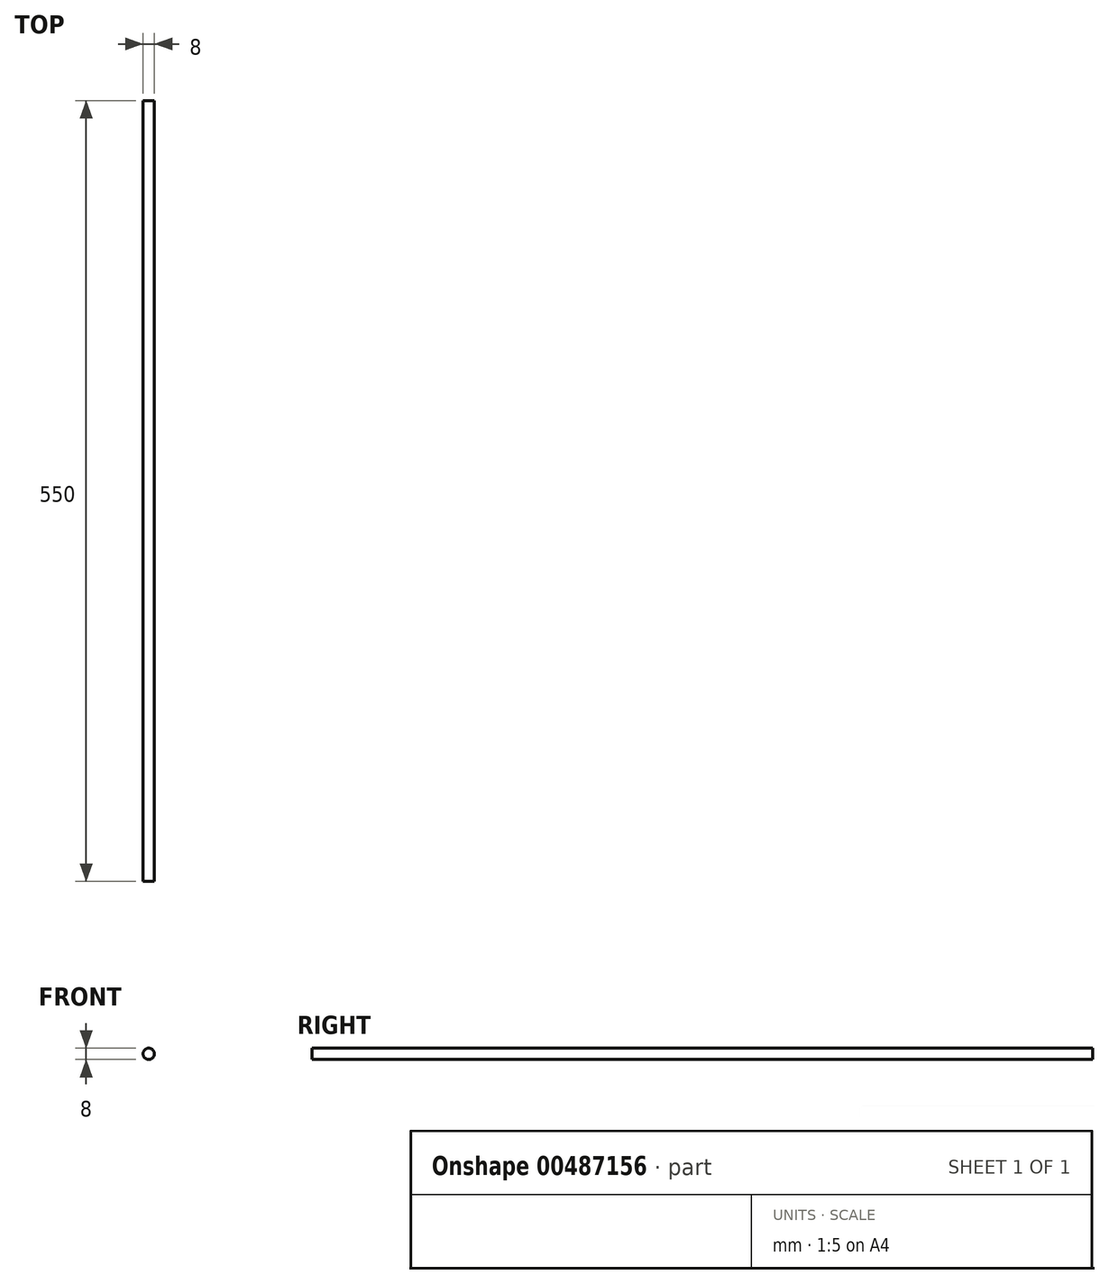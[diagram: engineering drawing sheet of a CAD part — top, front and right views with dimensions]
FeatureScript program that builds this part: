
annotation { "Feature Type Name" : "Feature", "Feature Type Description" : "" }
export const myFeature = defineFeature(function(context is Context, id is Id, definition is map)
    precondition{}
    {
        {
            var Q0;
            Q0=qCreatedBy(makeId("Front.planeOp"),FACE);
            var sketch = newSketch(context, id + "F0", { "sketchPlane" : qUnion([Q0])});
            skCircle(sketch, "E0", {"center": v(0, 0) * mm, "radius": 4 * mm});
            skSolve(sketch);
        }
        {
            var Q0;
            Q0 = qSketchRegion(id + "F0", true);
            extrude(context, id + "F1", {"entities" : qUnion([Q0]), "depth" : 275 * mm, "hasSecondDirection" : true, "secondDirectionOppositeDirection" : true, "secondDirectionDepth" : 275 * mm});
        }
    });
